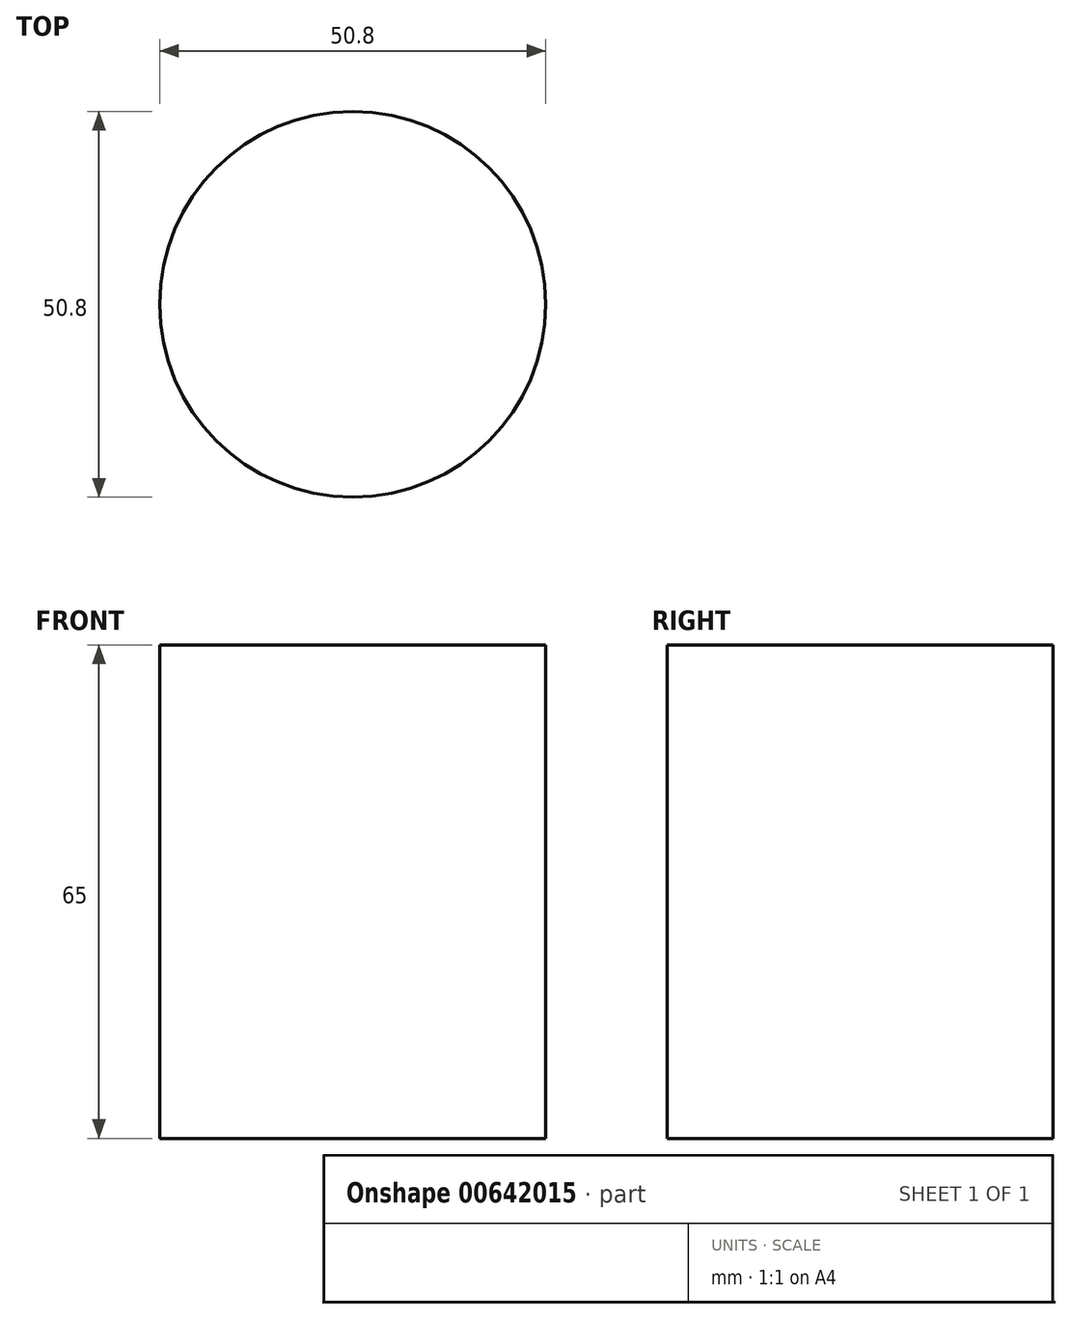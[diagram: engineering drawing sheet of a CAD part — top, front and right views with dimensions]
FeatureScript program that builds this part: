
annotation { "Feature Type Name" : "Feature", "Feature Type Description" : "" }
export const myFeature = defineFeature(function(context is Context, id is Id, definition is map)
    precondition{}
    {
        {
            var Q0;
            Q0=qCreatedBy(makeId("Top.planeOp"),FACE);
            var sketch = newSketch(context, id + "F0", { "sketchPlane" : qUnion([Q0])});
            skCircle(sketch, "E0", {"center": v(0, 0) * mm, "radius": 25.4 * mm});
            skSolve(sketch);
        }
        {
            var Q0;
            Q0 = qSketchRegion(id + "F0", true);
            extrude(context, id + "F1", {"entities" : qUnion([Q0]), "depth" : 65 * mm, "offsetDistance" : 25.4 * mm});
        }
    });
